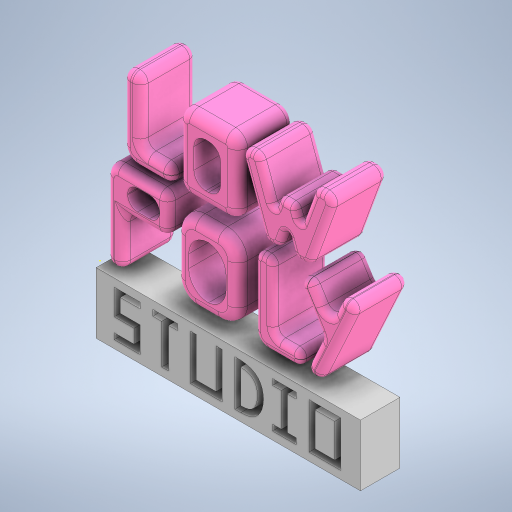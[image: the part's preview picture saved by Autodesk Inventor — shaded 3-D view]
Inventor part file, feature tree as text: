
AUTODESK INVENTOR PART (.ipt)
format: ipt  version: 2024.1 (Build 281209000, 209)  size: 1,076,224 bytes
history: native  units: mm
features: fillet x23, sketch x5, extrude x4, projected_geometry x1
ambient origin geometry x8: Origin, YZ Plane, XZ Plane, XY Plane, X Axis, Y Axis, Z Axis, Center Point
bodies: Solid2 (feature_tree)
feature tree (33):
  extrude  "Extrusion6"  Depth=10.0mm TaperAngle=0.0deg
  extrude  "Extrusion1"  Depth=90.0mm
  extrude  "Extrusion7"  Depth=1.0mm
  fillet  "Fillet1"  Radius=19.198622mm
  fillet  "Fillet2"  Radius=10.0mm
  fillet  "Fillet3"  Radius=28.0mm
  fillet  "Fillet4"  [1 undecoded]
  fillet  "Fillet5"  Radius=4.0mm
  fillet  "Fillet6"  Radius=5.0mm
  fillet  "Fillet7"  Radius=5.0mm
  fillet  "Fillet8"  Radius=10.0mm
  fillet  "Fillet9"  Radius=10.0mm
  fillet  "Fillet10"  Radius=5.0mm
  fillet  "Fillet11"  Radius=3.5mm
  fillet  "Fillet12"  Radius=3.0mm
  fillet  "Fillet13"  Radius=6.0mm
  fillet  "Fillet14"  Radius=3.5mm
  fillet  "Fillet15"  Radius=3.5mm
  fillet  "Fillet16"  Radius=4.0mm
  fillet  "Fillet17"  Radius=4.0mm
  fillet  "Fillet18"  Radius=7.0mm
  fillet  "Fillet19"  Radius=6.0mm
  fillet  "Fillet20"  Radius=6.0mm
  fillet  "Fillet21"  Radius=5.0mm
  fillet  "Fillet22"  Radius=4.0mm
  fillet  "Fillet23"  Radius=1.0mm
  sketch  "Sketch8"  dims[d61=3.0mm d62=3.0mm]
  extrude  "Extrusion8"  Depth=3.0mm
  sketch  "Sketch1"  dims[d0=40.0mm d4=10.0mm d5=0.0mm]
  sketch  "Sketch6"  dims[d24=160.0mm d25=90.0mm]
  projected_geometry  "Projected Loop1"
  sketch  "Sketch7"  dims[d26=90.0mm d27=0.0mm d28=19.198622mm d29=19.198622mm d31=10.0mm d39=28.0mm d40=0.0mm d41=0.0mm d42=4.0mm d43=5.0mm d44=5.0mm d45=10.0mm d46=10.0mm d47=5.0mm d48=3.5mm d49=3.0mm d50=6.0mm d51=3.5mm d52=3.5mm d53=4.0mm d54=4.0mm d55=7.0mm d56=6.0mm d57=6.0mm d58=5.0mm d59=4.0mm d60=1.0mm]
  sketch  "Sketch9"  dims[d63=19.198622mm d64=7.056118mm d65=7.5mm d66=6.0mm d67=3.0mm d69=3.931055mm d70=3.9mm d71=3.0mm d72=3.0mm d73=3.0mm d74=3.0mm d76=3.0mm d77=7.0mm d78=7.0mm d79=3.5mm d80=4.5mm d81=4.5mm d82=3.0mm d83=3.0mm d84=3.0mm d85=10.0mm d86=4.0mm d87=4.0mm d88=4.0mm d90=5.0mm d91=4.0mm d92=3.0mm d93=4.5mm d94=4.5mm d97=3.0mm d98=3.0mm d99=3.0mm d100=10.0mm d101=10.0mm d102=6.5mm d103=6.5mm d104=6.5mm d105=8.067383mm d106=5.308861mm d107=8.0mm d108=6.5mm d109=20.0mm d110=0.0mm d111=13.0mm d112=9.163248mm]
note: 1 required parameter value undecoded (feature->parameter linkage not recoverable at this tier; creation-order binding heuristic only, values carry confidence <= 0.55)
